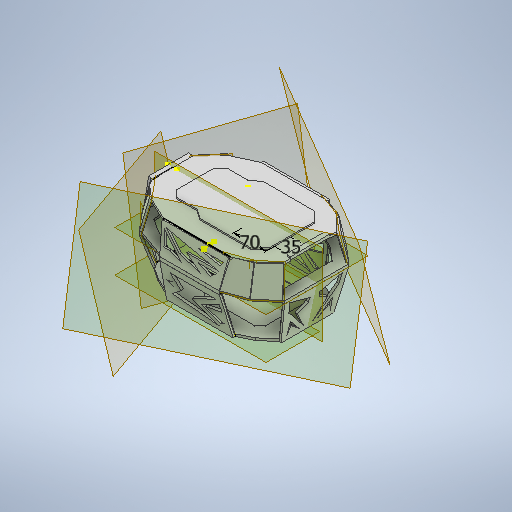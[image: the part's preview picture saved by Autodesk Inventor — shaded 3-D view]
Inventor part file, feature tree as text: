
AUTODESK INVENTOR PART (.ipt)
format: ipt  version: 2025.2 (Build 292293000, 293)  size: 6,089,216 bytes
history: native  units: mm
features: sketch x45, extrude x35, other x23, plane x17, loft x11, mirror x2, chamfer x2
ambient origin geometry x8: Origin, YZ Plane, XZ Plane, XY Plane, X Axis, Y Axis, Z Axis, Center Point
bodies: Body1 (feature_tree)
feature tree (135):
  extrude  "Extrusion2"  Depth=45.0mm
  extrude  "Extrusion3"  Depth=40.0mm
  plane  "Work Plane3"
  extrude  "Extrusion4"  Depth=145.0mm
  extrude  "Extrusion5"  Depth=55.0mm
  plane  "Work Plane4"
  extrude  "Extrusion6"  Depth=40.0mm
  sketch  "Sketch8"  dims[d17=165.0deg d18=15.0mm]
  sketch  "Sketch9"  dims[d20=10.0mm d21=40.0mm]
  sketch  "Sketch10"  dims[d22=5.0mm d23=5.0mm]
  loft  "Loft1"
  loft  "Loft2"
  extrude  "Extrusion7"  Depth=5.0mm
  extrude  "Extrusion8"  TaperAngle=90.0deg  [1 undecoded]
  extrude  "Extrusion9"  Depth=30.0mm
  sketch  "Sketch14"  dims[d30=45.0mm d31=20.0mm]
  sketch  "Sketch15"  dims[d32=45.0deg d39=5.0mm d40=0.0mm]
  sketch  "Sketch16"  dims[d41=3.0mm d42=3.0mm d43=0.0mm d44=0.0mm d45=150.0mm]
  loft  "Loft3"
  loft  "Loft4"
  loft  "Loft5"
  extrude  "Extrusion10"  Depth=3.0mm
  extrude  "Extrusion11"  Depth=10.0mm
  extrude  "Extrusion12"  Depth=10.0mm
  extrude  "Extrusion13"  Depth=10.0mm
  extrude  "Extrusion14"  Depth=10.0mm
  loft  "Loft7"
  loft  "Loft8"
  sketch  "Sketch22"  dims[d57=10.0mm d58=10.0mm]
  plane  "Work Plane5"
  extrude  "Extrusion15"  Depth=3.0mm TaperAngle=0.0deg
  plane  "Work Plane6"
  extrude  "Extrusion16"  Depth=10.0mm
  extrude  "Extrusion17"  Depth=50.0mm
  plane  "Work Plane7"
  extrude  "Extrusion18"  Depth=50.0mm
  sketch  "Sketch28"  dims[d71=27.925268mm d72=10.0mm]
  extrude  "Extrusion19"  Depth=10.0mm
  extrude  "Extrusion20"  Depth=60.0mm
  extrude  "Extrusion21"  Depth=5.0mm TaperAngle=0.0deg
  extrude  "Extrusion22"  TaperAngle=0.0deg  [1 undecoded]
  extrude  "Extrusion23"  TaperAngle=0.0deg  [1 undecoded]
  extrude  "Extrusion24"  Depth=4.0mm TaperAngle=0.0deg
  extrude  "Extrusion25"  TaperAngle=0.0deg  [1 undecoded]
  extrude  "Extrusion26"  TaperAngle=0.0deg  [1 undecoded]
  extrude  "Extrusion27"  TaperAngle=0.0deg  [1 undecoded]
  plane  "Work Plane8"
  mirror  "Mirror1"
  loft  "Loft9"
  loft  "Loft10"
  loft  "Loft11"
  loft  "Loft12"
  plane  "Work Plane14"
  plane  "Work Plane15"
  extrude  "Extrusion28"  TaperAngle=0.0deg  [1 undecoded]
  extrude  "Extrusion29"  Depth=4.0mm TaperAngle=0.0deg
  plane  "Work Plane16"
  extrude  "Extrusion30"  Depth=92.689mm
  mirror  "Mirror2"
  extrude  "Extrusion31"  Depth=70.0mm
  sketch  "Sketch42"  dims[d126=4.0mm d127=0.0mm d128=4.0mm d129=0.0mm]
  extrude  "Extrusion32"  Depth=10.0mm
  extrude  "Extrusion33"  Depth=70.0mm
  extrude  "Extrusion34"  Depth=35.0mm
  extrude  "Extrusion35"  Depth=10.0mm TaperAngle=0.0deg
  chamfer  "Chamfer1"  Distance=70.0mm
  extrude  "Extrusion36"  Depth=3.0mm
  chamfer  "Chamfer2"  Distance=17.5mm
  sketch  "Sketch48"  dims[d142=90.0deg d143=23.0mm d144=0.0mm d145=70.0mm d146=3.0mm d147=17.5mm d148=0.0mm d149=25.0mm d150=30.0mm d151=15.0deg d152=90.0deg d153=5.0mm d154=20.0mm d155=90.0deg d156=4.363323mm d157=17.5mm d158=0.0mm d159=25.0mm d160=165.0deg d161=40.0mm d162=150.0deg d163=50.0mm d164=1.745329mm d165=40.0mm d166=5.0mm d167=40.0mm d168=30.543262mm d169=17.5mm d170=0.0mm d171=10.0mm d172=100.0mm d173=150.0deg d174=40.0mm d175=19.198622mm d176=100.0mm d177=70.0mm d178=30.0deg d179=100.0mm d180=10.0mm d181=10.0mm d182=10.0mm d183=4.363323mm d184=40.0mm d185=40.0mm d186=6.981317mm d187=20.0mm d188=24.43461mm d189=16.0mm d190=10.0mm d191=0.0mm d192=80.0mm d193=24.43461mm d194=120.0mm d195=30.0deg d196=40.0mm d197=30.0deg d198=50.0mm d199=10.0mm d200=50.0mm d201=55.0mm d202=1.745329mm d203=30.0mm d204=27.925268mm d205=40.0mm d206=5.0mm d207=30.0mm d208=30.0mm d209=17.453293mm d210=60.0mm d211=30.0mm d212=50.0mm d213=0.0mm d214=10.0mm d215=10.0mm d216=10.0mm d217=10.0mm d218=90.0deg d219=10.0mm d220=20.0mm d221=10.0mm d222=17.453293mm d223=25.0mm d224=22.68928mm d225=70.0mm d226=10.0mm d227=40.0mm d228=22.68928mm d229=20.0mm d230=75.0deg d231=50.0mm d232=0.0mm d233=5.0mm d234=0.0mm d235=5.0mm d236=0.0mm d238=0.0mm d239=90.0deg d240=0.0mm d241=90.0deg d242=0.0mm d243=90.0deg d244=0.0mm d245=90.0deg d246=0.0mm d247=90.0deg d248=0.0mm d249=90.0deg d250=0.0mm d251=90.0deg d252=0.0mm d253=90.0deg d254=3.0mm d255=0.0mm d256=3.0mm d257=0.0mm d258=3.0mm d259=0.0mm d260=30.0mm d261=50.0mm d262=90.0mm d263=30.0mm d264=5.0mm d265=0.0mm d266=20.0mm d267=100.0mm d268=20.0mm d269=100.0mm d270=30.0mm d271=40.0mm d272=30.0mm d273=5.0mm d274=5.0mm d275=0.0mm d276=0.0mm d277=10.0mm d278=10.0mm d279=30.0mm d280=0.0mm d281=20.0mm d282=20.0mm d283=20.0mm d284=90.0deg d285=10.0mm d286=0.0mm d287=20.0mm d288=100.0mm d289=0.0mm d290=10.0mm d291=10.0mm d292=10.0mm d293=0.0mm d294=6.0mm d295=2.0mm d296=45.0deg d297=20.0mm d298=13.0mm d299=20.0mm d300=13.0mm d301=20.0mm d302=13.0mm d303=20.0mm d304=13.0mm d305=20.0mm d306=0.0mm d307=20.0mm d308=2.0mm d309=45.0deg d310=140.0mm d311=10.0mm]
  sketch  "Sketch1"  dims[d6=115.0mm d8=45.0mm]
  other  "Image1"
  sketch  "Sketch3"  dims[d9=45.0deg d10=40.0mm]
  sketch  "Sketch4"  dims[d11=27.925268mm d12=145.0mm]
  sketch  "Sketch5"  dims[d13=27.052603mm d14=55.0mm]
  sketch  "Sketch6"  dims[d15=27.052603mm d16=40.0mm]
  other  "Edges1"
  other  "Edges2"
  other  "Edges3"
  other  "Edges4"
  sketch  "Sketch11"  dims[d24=40.0mm d25=90.0deg]
  sketch  "Sketch12"  dims[d26=30.0mm d27=110.0mm]
  sketch  "Sketch13"  dims[d28=25.0mm d29=25.307274mm]
  other  "Edges5"
  other  "Edges6"
  other  "Edges7"
  other  "Edges8"
  other  "Edges9"
  other  "Edges10"
  sketch  "Sketch17"  dims[d46=10.0mm d48=10.0mm]
  sketch  "Sketch18"  dims[d49=10.0mm d50=22.68928mm]
  sketch  "Sketch19"  dims[d51=10.0mm d52=10.0mm]
  sketch  "Sketch20"  dims[d53=10.0mm d54=10.0mm]
  sketch  "Sketch21"  dims[d55=10.0mm d56=10.0mm]
  other  "Edges13"
  other  "Edges14"
  other  "Edges15"
  other  "Edges16"
  sketch  "Sketch23"  dims[d59=5.0mm d60=0.0mm d61=3.0mm d62=3.0mm d63=0.0mm d64=0.0mm]
  sketch  "Sketch24"  dims[d65=-90.0mm d66=10.0mm]
  sketch  "Sketch25"  dims[d67=70.0mm d68=50.0mm]
  sketch  "Sketch26"  dims[d69=22.68928mm d70=50.0mm]
  sketch  "Sketch29"  dims[d73=50.0mm d74=60.0mm]
  sketch  "Sketch30"  dims[d75=70.0mm d76=5.0mm d77=0.0mm]
  sketch  "Sketch31"  dims[d78=0.0mm d79=90.0deg d80=0.0mm d81=90.0deg]
  sketch  "Sketch32"  dims[d82=0.0mm d83=90.0deg d84=0.0mm d85=90.0deg]
  sketch  "Sketch33"  dims[d86=4.0mm d87=0.0mm d88=4.0mm d89=0.0mm]
  sketch  "Sketch34"  dims[d90=4.0mm d91=0.0mm d92=0.0mm d93=90.0deg]
  sketch  "Sketch35"  dims[d94=0.0mm d95=90.0deg d96=0.0mm d97=90.0deg]
  sketch  "Sketch36"  dims[d98=0.0mm d99=90.0deg d100=0.0mm d101=90.0deg]
  sketch  "Sketch37"  dims[d102=0.0mm d103=90.0deg d104=4.0mm d105=0.0mm]
  plane  "Work Plane9"
  plane  "Work Plane10"
  plane  "Work Plane11"
  plane  "Work Plane12"
  plane  "Work Plane13"
  other  "Edges17"
  other  "Edges18"
  other  "Edges19"
  other  "Edges20"
  other  "Edges21"
  other  "Edges22"
  other  "Edges23"
  other  "Edges24"
  sketch  "Sketch38"  dims[d106=4.0mm d107=0.0mm d108=4.0mm d109=0.0mm]
  sketch  "Sketch39"  dims[d110=4.0mm d111=0.0mm d112=4.0mm d113=0.0mm]
  sketch  "Sketch40"  dims[d118=0.0mm d119=90.0deg d120=0.0mm d121=90.0deg]
  plane  "Work Plane17"
  plane  "Work Plane18"
  plane  "Work Plane19"
  sketch  "Sketch41"  dims[d122=0.0mm d123=90.0deg d124=0.0mm d125=90.0deg]
  sketch  "Sketch43"  dims[d130=4.0mm d131=0.0mm d132=92.689mm]
  sketch  "Sketch44"  dims[d133=4.0mm d134=0.0mm d135=70.0mm]
  sketch  "Sketch45"  dims[d136=35.0mm d137=10.0mm]
  sketch  "Sketch46"  dims[d138=50.0mm d139=70.0mm]
  sketch  "Sketch47"  dims[d140=50.0mm d141=35.0mm]
note: 7 required parameter values undecoded (feature->parameter linkage not recoverable at this tier; creation-order binding heuristic only, values carry confidence <= 0.55)
